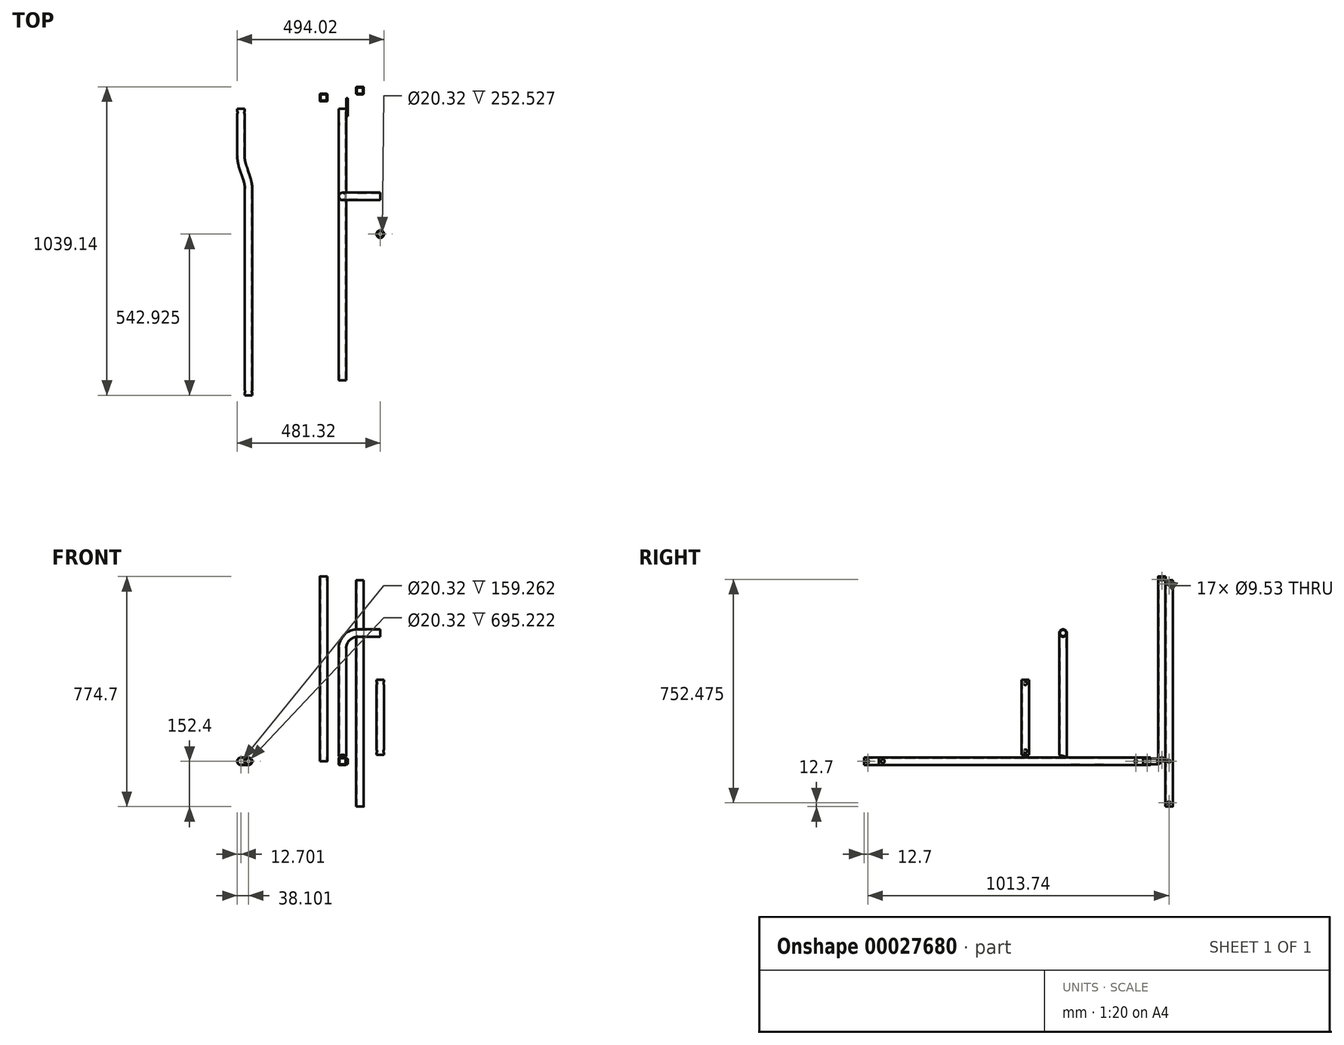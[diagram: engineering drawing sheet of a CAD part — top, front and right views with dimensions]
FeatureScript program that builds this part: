
annotation { "Feature Type Name" : "Feature", "Feature Type Description" : "" }
export const myFeature = defineFeature(function(context is Context, id is Id, definition is map)
    precondition{}
    {
        {
            var Q0;
            Q0=qCreatedBy(makeId("Front.planeOp"),FACE);
            var sketch = newSketch(context, id + "F0", { "sketchPlane" : qUnion([Q0])});
            skLineSegment(sketch, "E0.bottom", {"start": v(-9.53, 12.7) * mm, "end": v(9.53, 12.7) * mm});
            skLineSegment(sketch, "E0.top", {"start": v(-9.53, -12.7) * mm, "end": v(9.53, -12.7) * mm});
            skLineSegment(sketch, "E0.left", {"start": v(-12.7, 9.52) * mm, "end": v(-12.7, -9.52) * mm});
            skLineSegment(sketch, "E0.right", {"start": v(12.7, 9.52) * mm, "end": v(12.7, -9.52) * mm});
            skLineSegment(sketch, "E1", {"start": v(-12.7, 12.7) * mm, "end": v(12.7, -12.7) * mm, "construction": true});
            skPoint(sketch, "E2.visualSharp", {"position": v(-12.7, 12.7) * mm});
            skArc(sketch, "E2.filletArc", {"start": v(-9.53, 12.7) * mm, "mid": v(-11.77, 11.77) * mm, "end": v(-12.7, 9.52) * mm});
            skPoint(sketch, "E3.visualSharp", {"position": v(-12.7, -12.7) * mm});
            skArc(sketch, "E3.filletArc", {"start": v(-12.7, -9.52) * mm, "mid": v(-11.77, -11.77) * mm, "end": v(-9.53, -12.7) * mm});
            skPoint(sketch, "E4.visualSharp", {"position": v(12.7, -12.7) * mm});
            skArc(sketch, "E4.filletArc", {"start": v(9.53, -12.7) * mm, "mid": v(11.77, -11.77) * mm, "end": v(12.7, -9.52) * mm});
            skPoint(sketch, "E5.visualSharp", {"position": v(12.7, 12.7) * mm});
            skArc(sketch, "E5.filletArc", {"start": v(12.7, 9.52) * mm, "mid": v(11.77, 11.77) * mm, "end": v(9.53, 12.7) * mm});
            skLineSegment(sketch, "E6.0", {"start": v(10.16, 10.16) * mm, "end": v(10.16, -10.16) * mm});
            skLineSegment(sketch, "E6.1", {"start": v(-10.16, 10.16) * mm, "end": v(10.16, 10.16) * mm});
            skLineSegment(sketch, "E6.2", {"start": v(-10.16, 10.16) * mm, "end": v(-10.16, -10.16) * mm});
            skLineSegment(sketch, "E6.3", {"start": v(-10.16, -10.16) * mm, "end": v(10.16, -10.16) * mm});
            skSolve(sketch);
        }
        {
            var Q0;
            Q0=makeQuery(id+"F0.imprint","IMPRINT",FACE,{"disambiguationData":[TD([[makeQuery(id+"F0.imprint","IMPRINT",EDGE,{"derivedFrom":sQuery(id+"F0.wireOp",EDGE,"E0.bottom")}),-1.0]])]});
            extrude(context, id + "F1", {"entities" : qUnion([Q0]), "depth" : 914.4 * mm});
        }
        {
            var Q0;
            Q0=makeQuery(id+"F1.opExtrude","SWEPT_FACE",FACE,{"disambiguationData":[OSD([sQuery(id+"F0.wireOp",EDGE,"E0.right")])]});
            var sketch = newSketch(context, id + "F2", { "sketchPlane" : qUnion([Q0])});
            skCircle(sketch, "E7", {"center": v(-50.8, 0) * mm, "radius": 4.76 * mm});
            skSolve(sketch);
        }
        {
            var Q0;
            Q0=makeQuery(id+"F2.imprint","IMPRINT",FACE,{"disambiguationData":[TD([[makeQuery(id+"F2.imprint","IMPRINT",EDGE,{"derivedFrom":sQuery(id+"F2.wireOp",EDGE,"E7")}),1.0]])]});
            extrude(context, id + "F3", {"entities" : qUnion([Q0]), "operationType" : NewBodyOperationType.REMOVE, "endBound" : BoundingType.THROUGH_ALL, "oppositeDirection" : true, "depth" : 25.4 * mm});
        }
        {
            var Q0;
            Q0=makeQuery(id+"F1.opExtrude","SWEPT_FACE",FACE,{"disambiguationData":[OSD([sQuery(id+"F0.wireOp",EDGE,"E0.bottom")])]});
            var sketch = newSketch(context, id + "F4", { "sketchPlane" : qUnion([Q0])});
            skCircle(sketch, "E8", {"center": v(0, -295.27) * mm, "radius": 12.7 * mm});
            skCircle(sketch, "E9.0", {"center": v(0, -295.27) * mm, "radius": 10.16 * mm});
            skSolve(sketch);
        }
        {
            var Q0;
            Q0 = qSketchRegion(id + "F4", true);
            extrude(context, id + "F5", {"entities" : qUnion([Q0]), "depth" : 355.6 * mm});
        }
        {
            var Q0;
            Q0=makeQuery(id+"F1.opExtrude","SWEPT_FACE",FACE,{"disambiguationData":[OSD([sQuery(id+"F0.wireOp",EDGE,"E0.right")])]});
            var sketch = newSketch(context, id + "F6", { "sketchPlane" : qUnion([Q0])});
            skCircle(sketch, "E10", {"center": v(-901.7, 0) * mm, "radius": 6.35 * mm});
            skPoint(sketch, "E10.centerSnap0", {"position": v(-914.4, 0) * mm});
            skSolve(sketch);
        }
        {
            var Q0;
            Q0 = qSketchRegion(id + "F6", true);
            extrude(context, id + "F7", {"entities" : qUnion([Q0]), "operationType" : NewBodyOperationType.REMOVE, "endBound" : BoundingType.THROUGH_ALL, "oppositeDirection" : true, "depth" : 25.4 * mm});
        }
        {
            var Q0;
            Q0=makeQuery(id+"F1.opExtrude","SWEPT_FACE",FACE,{"disambiguationData":[OSD([sQuery(id+"F0.wireOp",EDGE,"E0.right")])]});
            var sketch = newSketch(context, id + "F8", { "sketchPlane" : qUnion([Q0])});
            skLineSegment(sketch, "E11", {"start": v(-388.7, 12.7) * mm, "end": v(-275.6, 12.7) * mm});
            skLineSegment(sketch, "E12", {"start": v(-275.6, 12.7) * mm, "end": v(-388.7, 43) * mm});
            skLineSegment(sketch, "E13", {"start": v(-388.7, 43) * mm, "end": v(-388.7, 12.7) * mm});
            skPoint(sketch, "E14", {"position": v(-275.6, 12.7) * mm});
            skSolve(sketch);
        }
        {
            var Q0;
            Q0 = qSketchRegion(id + "F8", true);
            extrude(context, id + "F9", {"entities" : qUnion([Q0]), "operationType" : NewBodyOperationType.REMOVE, "endBound" : BoundingType.THROUGH_ALL, "oppositeDirection" : true, "depth" : 25.4 * mm});
        }
        {
            var Q0;
            Q0=qCreatedBy(makeId("Top.planeOp"),FACE);
            var sketch = newSketch(context, id + "F10", { "sketchPlane" : qUnion([Q0])});
            skLineSegment(sketch, "E15.bottom", {"start": v(-73.82, 50.02) * mm, "end": v(-53.5, 50.02) * mm});
            skLineSegment(sketch, "E15.top", {"start": v(-73.82, 24.62) * mm, "end": v(-53.5, 24.62) * mm});
            skLineSegment(sketch, "E15.left", {"start": v(-76.36, 47.48) * mm, "end": v(-76.36, 27.16) * mm});
            skLineSegment(sketch, "E15.right", {"start": v(-50.96, 47.48) * mm, "end": v(-50.96, 27.16) * mm});
            skPoint(sketch, "E16.visualSharp", {"position": v(-76.36, 50.02) * mm});
            skArc(sketch, "E16.filletArc", {"start": v(-73.82, 50.02) * mm, "mid": v(-75.62, 49.27) * mm, "end": v(-76.36, 47.48) * mm});
            skPoint(sketch, "E17.visualSharp", {"position": v(-50.96, 50.02) * mm});
            skArc(sketch, "E17.filletArc", {"start": v(-50.96, 47.48) * mm, "mid": v(-51.7, 49.27) * mm, "end": v(-53.5, 50.02) * mm});
            skPoint(sketch, "E18.visualSharp", {"position": v(-50.96, 24.62) * mm});
            skArc(sketch, "E18.filletArc", {"start": v(-53.5, 24.62) * mm, "mid": v(-51.7, 25.36) * mm, "end": v(-50.96, 27.16) * mm});
            skPoint(sketch, "E19.visualSharp", {"position": v(-76.36, 24.62) * mm});
            skArc(sketch, "E19.filletArc", {"start": v(-76.36, 27.16) * mm, "mid": v(-75.62, 25.36) * mm, "end": v(-73.82, 24.62) * mm});
            skLineSegment(sketch, "E20.0", {"start": v(-73.82, 47.48) * mm, "end": v(-53.5, 47.48) * mm});
            skLineSegment(sketch, "E20.1", {"start": v(-73.82, 47.48) * mm, "end": v(-73.82, 27.16) * mm});
            skLineSegment(sketch, "E20.2", {"start": v(-73.82, 27.16) * mm, "end": v(-53.5, 27.16) * mm});
            skLineSegment(sketch, "E20.3", {"start": v(-53.5, 47.48) * mm, "end": v(-53.5, 27.16) * mm});
            skSolve(sketch);
        }
        {
            var Q0;
            Q0 = qSketchRegion(id + "F10", true);
            extrude(context, id + "F11", {"entities" : qUnion([Q0]), "depth" : 622.3 * mm});
        }
        {
            var Q0;
            Q0=makeQuery(id+"F11.opExtrude","SWEPT_FACE",FACE,{"disambiguationData":[OSD([sQuery(id+"F10.wireOp",EDGE,"E15.right")])]});
            var sketch = newSketch(context, id + "F12", { "sketchPlane" : qUnion([Q0])});
            skCircle(sketch, "E21", {"center": v(37.32, 612.78) * mm, "radius": 4.76 * mm});
            skPoint(sketch, "E22", {"position": v(37.32, 622.3) * mm});
            skCircle(sketch, "E23", {"center": v(37.32, 9.53) * mm, "radius": 4.76 * mm});
            skPoint(sketch, "E23.centerSnap0", {"position": v(37.32, 0) * mm});
            skSolve(sketch);
        }
        {
            var Q0;
            Q0 = qSketchRegion(id + "F12", true);
            extrude(context, id + "F13", {"entities" : qUnion([Q0]), "operationType" : NewBodyOperationType.REMOVE, "endBound" : BoundingType.THROUGH_ALL, "oppositeDirection" : true, "depth" : 25.4 * mm});
        }
        {
            var Q0;
            Q0=makeQuery(id+"F1.opExtrude","SWEPT_FACE",FACE,{"disambiguationData":[OSD([sQuery(id+"F0.wireOp",EDGE,"E0.right")])]});
            var sketch = newSketch(context, id + "F14", { "sketchPlane" : qUnion([Q0])});
            skLineSegment(sketch, "E24.bottom", {"start": v(-25.4, 9.52) * mm, "end": v(25.4, 9.52) * mm});
            skLineSegment(sketch, "E24.top", {"start": v(-25.4, -9.52) * mm, "end": v(25.4, -9.52) * mm});
            skLineSegment(sketch, "E24.left", {"start": v(-25.4, 9.52) * mm, "end": v(-25.4, -9.52) * mm});
            skLineSegment(sketch, "E24.right", {"start": v(34.93, 0) * mm, "end": v(34.93, 0) * mm});
            skCircle(sketch, "E25", {"center": v(25.4, 0) * mm, "radius": 4.76 * mm});
            skPoint(sketch, "E26.visualSharp", {"position": v(34.93, 9.52) * mm});
            skArc(sketch, "E26.filletArc", {"start": v(34.93, 0) * mm, "mid": v(32.14, 6.74) * mm, "end": v(25.4, 9.52) * mm});
            skPoint(sketch, "E27.visualSharp", {"position": v(34.93, -9.52) * mm});
            skArc(sketch, "E27.filletArc", {"start": v(25.4, -9.52) * mm, "mid": v(32.14, -6.74) * mm, "end": v(34.93, 0) * mm});
            skSolve(sketch);
        }
        {
            var Q0;
            Q0 = qSketchRegion(id + "F14", true);
            extrude(context, id + "F15", {"entities" : qUnion([Q0]), "depth" : 4.76 * mm});
        }
        {
            var Q0;
            Q0=qCreatedBy(makeId("Top.planeOp"),FACE);
            var sketch = newSketch(context, id + "F16", { "sketchPlane" : qUnion([Q0])});
            skLineSegment(sketch, "E28.bottom", {"start": v(49.22, 48.54) * mm, "end": v(68.27, 48.54) * mm});
            skLineSegment(sketch, "E28.top", {"start": v(49.22, 73.94) * mm, "end": v(68.27, 73.94) * mm});
            skLineSegment(sketch, "E28.left", {"start": v(46.04, 51.71) * mm, "end": v(46.04, 70.76) * mm});
            skLineSegment(sketch, "E28.right", {"start": v(71.44, 51.71) * mm, "end": v(71.44, 70.76) * mm});
            skPoint(sketch, "E29.visualSharp", {"position": v(46.04, 48.54) * mm});
            skArc(sketch, "E29.filletArc", {"start": v(46.04, 51.71) * mm, "mid": v(46.97, 49.47) * mm, "end": v(49.22, 48.54) * mm});
            skPoint(sketch, "E30.visualSharp", {"position": v(71.44, 48.54) * mm});
            skArc(sketch, "E30.filletArc", {"start": v(68.27, 48.54) * mm, "mid": v(70.51, 49.47) * mm, "end": v(71.44, 51.71) * mm});
            skPoint(sketch, "E31.visualSharp", {"position": v(71.44, 73.94) * mm});
            skArc(sketch, "E31.filletArc", {"start": v(71.44, 70.76) * mm, "mid": v(70.51, 73) * mm, "end": v(68.27, 73.94) * mm});
            skPoint(sketch, "E32.visualSharp", {"position": v(46.04, 73.94) * mm});
            skArc(sketch, "E32.filletArc", {"start": v(49.22, 73.94) * mm, "mid": v(46.97, 73) * mm, "end": v(46.04, 70.76) * mm});
            skLineSegment(sketch, "E33.0", {"start": v(48.58, 51.08) * mm, "end": v(48.58, 71.4) * mm});
            skLineSegment(sketch, "E33.1", {"start": v(48.58, 51.08) * mm, "end": v(68.9, 51.08) * mm});
            skLineSegment(sketch, "E33.2", {"start": v(68.9, 51.08) * mm, "end": v(68.9, 71.4) * mm});
            skLineSegment(sketch, "E33.3", {"start": v(48.58, 71.4) * mm, "end": v(68.9, 71.4) * mm});
            skSolve(sketch);
        }
        {
            var Q0;
            Q0=makeQuery(id+"F16.imprint","IMPRINT",FACE,{"disambiguationData":[TD([[makeQuery(id+"F16.imprint","IMPRINT",EDGE,{"derivedFrom":sQuery(id+"F16.wireOp",EDGE,"E28.bottom")}),1.0]])]});
            extrude(context, id + "F17", {"entities" : qUnion([Q0]), "depth" : 609.6 * mm, "hasSecondDirection" : true, "secondDirectionOppositeDirection" : true, "secondDirectionDepth" : 152.4 * mm});
        }
        {
            var Q0;
            Q0=makeQuery(id+"F17.opExtrude","SWEPT_FACE",FACE,{"disambiguationData":[OSD([sQuery(id+"F16.wireOp",EDGE,"E28.left")])]});
            var sketch = newSketch(context, id + "F18", { "sketchPlane" : qUnion([Q0])});
            skCircle(sketch, "E34", {"center": v(-61.24, 0) * mm, "radius": 4.76 * mm});
            skCircle(sketch, "E35", {"center": v(-61.24, -139.7) * mm, "radius": 4.76 * mm});
            skLineSegment(sketch, "E36", {"start": v(-61.24, -152.4) * mm, "end": v(-61.24, 609.6) * mm, "construction": true});
            skCircle(sketch, "E37", {"center": v(-61.24, 596.9) * mm, "radius": 4.76 * mm});
            skSolve(sketch);
        }
        {
            var Q0;
            Q0 = qSketchRegion(id + "F18", true);
            extrude(context, id + "F19", {"entities" : qUnion([Q0]), "operationType" : NewBodyOperationType.REMOVE, "oppositeDirection" : true, "depth" : 25.4 * mm});
        }
        {
            var Q0;
            Q0=makeQuery(id+"F5.opExtrude","SWEPT_BODY",BODY,{"disambiguationData":[OSD([sQuery(id+"F4.wireOp",EDGE,"E8"),sQuery(id+"F4.wireOp",EDGE,"E9.0")])]});
            transform(context, id + "F20", {"entities" : qUnion([Q0]), "transformType" : TransformType.TRANSLATION_3D, "dx" : 127 * mm, "dy" : -127 * mm, "dz" : 0 * mm, "makeCopy" : true});
        }
        {
            var Q0;
            Q0=qCreatedBy(makeId("Right.planeOp"),FACE);
            var sketch = newSketch(context, id + "F21", { "sketchPlane" : qUnion([Q0])});
            skLineSegment(sketch, "E38", {"start": v(-422.27, 368.3) * mm, "end": v(-422.27, -39.06) * mm, "construction": true});
            skCircle(sketch, "E39", {"center": v(-422.27, 34.07) * mm, "radius": 5.9 * mm});
            skCircle(sketch, "E40", {"center": v(-422.27, 262.67) * mm, "radius": 5.9 * mm});
            skLineSegment(sketch, "E41.0", {"start": v(-434.97, 368.3) * mm, "end": v(-409.57, 368.3) * mm});
            skLineSegment(sketch, "E42.bottom", {"start": v(-434.97, 21.37) * mm, "end": v(-409.57, 21.37) * mm});
            skLineSegment(sketch, "E42.top", {"start": v(-434.97, 14.57) * mm, "end": v(-409.57, 14.57) * mm});
            skLineSegment(sketch, "E42.left", {"start": v(-434.97, 21.37) * mm, "end": v(-434.97, 14.57) * mm});
            skLineSegment(sketch, "E42.right", {"start": v(-409.57, 21.37) * mm, "end": v(-409.57, 14.57) * mm});
            skLineSegment(sketch, "E43.0", {"start": v(-434.97, 21.37) * mm, "end": v(-409.57, 14.57) * mm});
            skSolve(sketch);
        }
        {
            var Q0;
            Q0 = qSketchRegion(id + "F21", true);
            extrude(context, id + "F22", {"entities" : qUnion([Q0]), "operationType" : NewBodyOperationType.REMOVE, "endBound" : BoundingType.THROUGH_ALL, "depth" : 25.4 * mm, "hasSecondDirection" : true, "secondDirectionBound" : BoundingType.THROUGH_ALL, "secondDirectionOppositeDirection" : true, "secondDirectionDepth" : 25.4 * mm});
        }
        {
            var Q0;
            Q0=qCreatedBy(makeId("Top.planeOp"),FACE);
            var sketch = newSketch(context, id + "F23", { "sketchPlane" : qUnion([Q0])});
            skLineSegment(sketch, "E44", {"start": v(-341.62, 0) * mm, "end": v(-341.62, -159.26) * mm});
            skLineSegment(sketch, "E45", {"start": v(-336.72, -190.45) * mm, "end": v(-321.12, -238.8) * mm});
            skLineSegment(sketch, "E46", {"start": v(-316.22, -269.98) * mm, "end": v(-316.22, -965.2) * mm});
            skPoint(sketch, "E47.visualSharp", {"position": v(-341.62, -175.24) * mm});
            skArc(sketch, "E47.filletArc", {"start": v(-341.62, -159.26) * mm, "mid": v(-340.39, -175.05) * mm, "end": v(-336.72, -190.45) * mm});
            skPoint(sketch, "E48.visualSharp", {"position": v(-316.22, -254) * mm});
            skArc(sketch, "E48.filletArc", {"start": v(-316.22, -269.98) * mm, "mid": v(-317.45, -254.2) * mm, "end": v(-321.12, -238.8) * mm});
            skSolve(sketch);
        }
        {
            var Q0;
            Q0=sQuery(id+"F23.wireOp",EDGE,"E46");
            var Q1;
            Q1=sQuery(id+"F23.wireOp",VERTEX,"E46.end");
            cPlane(context, id + "F24", {"entities" : qUnion([Q0, Q1]), "cplaneType" : CPlaneType.LINE_POINT, "offset" : 152.4 * mm, "width" : 152.4 * mm, "height" : 152.4 * mm});
        }
        {
            var Q0;
            Q0=qCreatedBy(id+"F24.planeOp",FACE);
            var sketch = newSketch(context, id + "F25", { "sketchPlane" : qUnion([Q0])});
            skCircle(sketch, "E49", {"center": v(-316.22, 0) * mm, "radius": 12.7 * mm});
            skCircle(sketch, "E50.0", {"center": v(-316.22, 0) * mm, "radius": 10.16 * mm});
            skSolve(sketch);
        }
        {
            var Q0;
            Q0 = qSketchRegion(id + "F25", true);
            var Q1;
            Q1 = qConstructionFilter(qBodyType(qCreatedBy(id + "F23" ,EDGE), BodyType.WIRE), ConstructionObject.NO);
            sweep(context, id + "F26", {"profiles" : qUnion([Q0]), "path" : qUnion([Q1])});
        }
        {
            var Q0;
            Q0=qCreatedBy(makeId("Right.planeOp"),FACE);
            cPlane(context, id + "F27", {"entities" : qUnion([Q0]), "cplaneType" : CPlaneType.OFFSET, "offset" : 254 * mm, "oppositeDirection" : true, "width" : 152.4 * mm, "height" : 152.4 * mm});
        }
        {
            var Q0;
            Q0=qCreatedBy(id+"F27.planeOp",FACE);
            var sketch = newSketch(context, id + "F28", { "sketchPlane" : qUnion([Q0])});
            skLineSegment(sketch, "E51.0", {"start": v(0, -12.7) * mm, "end": v(0, 12.7) * mm});
            skCircle(sketch, "E52", {"center": v(-12.7, 0) * mm, "radius": 4.76 * mm});
            skPoint(sketch, "E52.centerSnap0", {"position": v(0, 0) * mm});
            skLineSegment(sketch, "E53.0", {"start": v(-965.2, -12.7) * mm, "end": v(-965.2, 12.7) * mm});
            skCircle(sketch, "E54", {"center": v(-952.5, 0) * mm, "radius": 4.76 * mm});
            skPoint(sketch, "E54.centerSnap0", {"position": v(-965.2, 0) * mm});
            skSolve(sketch);
        }
        {
            var Q0;
            Q0 = qSketchRegion(id + "F28", true);
            extrude(context, id + "F29", {"entities" : qUnion([Q0]), "operationType" : NewBodyOperationType.REMOVE, "endBound" : BoundingType.THROUGH_ALL, "oppositeDirection" : true, "depth" : 25.4 * mm});
        }
        {
            var Q0;
            Q0=makeQuery(id+"F20.opPattern","COPY",FACE,{"derivedFrom":makeQuery(id+"F5.opExtrude","CAP_FACE",FACE,{"disambiguationData":[OSD([sQuery(id+"F4.wireOp",EDGE,"E8"),sQuery(id+"F4.wireOp",EDGE,"E9.0")])],"isStart":false}),"instanceName":"1"});
            extrude(context, id + "F30", {"entities" : qUnion([Q0]), "operationType" : NewBodyOperationType.ADD, "depth" : 255.05 * mm});
        }
        {
            var Q0;
            Q0=qCreatedBy(id+"F27.planeOp",FACE);
            var sketch = newSketch(context, id + "F31", { "sketchPlane" : qUnion([Q0])});
            skLineSegment(sketch, "E55.bottom", {"start": v(-474.2, 900.3) * mm, "end": v(-361.02, 900.3) * mm});
            skLineSegment(sketch, "E55.top", {"start": v(-474.2, 273.9) * mm, "end": v(-361.02, 273.9) * mm});
            skLineSegment(sketch, "E55.left", {"start": v(-361.02, 900.3) * mm, "end": v(-361.02, 273.9) * mm});
            skLineSegment(sketch, "E55.right", {"start": v(-474.2, 900.3) * mm, "end": v(-474.2, 273.9) * mm});
            skSolve(sketch);
        }
        {
            var Q0;
            Q0 = qSketchRegion(id + "F31", true);
            extrude(context, id + "F32", {"entities" : qUnion([Q0]), "operationType" : NewBodyOperationType.REMOVE, "endBound" : BoundingType.THROUGH_ALL, "depth" : 25.4 * mm});
        }
        {
            var Q0;
            Q0=sQuery(id+"F4.wireOp",VERTEX,"E8.center");
            var Q1;
            Q1=qCreatedBy(makeId("Front.planeOp"),FACE);
            cPlane(context, id + "F33", {"entities" : qUnion([Q0, Q1]), "cplaneType" : CPlaneType.PLANE_POINT, "offset" : 25.4 * mm, "width" : 152.4 * mm, "height" : 152.4 * mm});
        }
        {
            var Q0;
            Q0=qCreatedBy(id+"F33.planeOp",FACE);
            var sketch = newSketch(context, id + "F34", { "sketchPlane" : qUnion([Q0])});
            skLineSegment(sketch, "E56", {"start": v(0, 368.3) * mm, "end": v(0, 381) * mm});
            skLineSegment(sketch, "E57", {"start": v(50.8, 431.8) * mm, "end": v(127, 431.8) * mm});
            skPoint(sketch, "E58.visualSharp", {"position": v(0, 431.8) * mm});
            skArc(sketch, "E58.filletArc", {"start": v(50.8, 431.8) * mm, "mid": v(14.88, 416.92) * mm, "end": v(0, 381) * mm});
            skSolve(sketch);
        }
        {
            var Q0;
            Q0=makeQuery(id+"F5.opExtrude","CAP_FACE",FACE,{"disambiguationData":[OSD([sQuery(id+"F4.wireOp",EDGE,"E8"),sQuery(id+"F4.wireOp",EDGE,"E9.0")])],"isStart":false});
            var Q1;
            Q1=sQuery(id+"F34.wireOp",EDGE,"E56");
            var Q2;
            Q2=sQuery(id+"F34.wireOp",EDGE,"E58.filletArc");
            var Q3;
            Q3=sQuery(id+"F34.wireOp",EDGE,"E57");
            sweep(context, id + "F35", {"operationType" : NewBodyOperationType.ADD, "profiles" : qUnion([Q0]), "path" : qUnion([Q1, Q2, Q3])});
        }
    });
